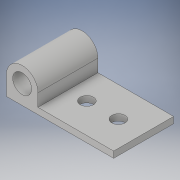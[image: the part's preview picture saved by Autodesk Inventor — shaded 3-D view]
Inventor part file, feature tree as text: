
AUTODESK INVENTOR PART (.ipt)
format: ipt  version: 2019 (Build 230136000, 136)  size: 126,976 bytes
history: native  units: mm
features: other x7, extrude x3, sketch x3
ambient origin geometry x8: Origin, YZ Plane, XZ Plane, XY Plane, X Axis, Y Axis, Z Axis, Center Point
bodies: Solid1 (feature_tree)
feature tree (13):
  extrude  "Extrusion1"  Depth=9.5mm TaperAngle=0.0deg
  extrude  "Extrusion2"  [1 undecoded]
  extrude  "Extrusion3"  [1 undecoded]
  other  "A_XY"
  other  "A_YZ"
  other  "A_ZX"
  other  "A_X"
  other  "A_Y"
  other  "A_Z"
  other  "A_Center"
  sketch  "Sketch_1"  dims[d0=9.5mm d1=0.0mm d2=9.5mm d3=0.0mm]
  sketch  "Sketch_2"  dims[d4=9.5mm d5=0.0mm]
  sketch  "Sketch_3"
note: 2 required parameter values undecoded (feature->parameter linkage not recoverable at this tier; creation-order binding heuristic only, values carry confidence <= 0.55)
